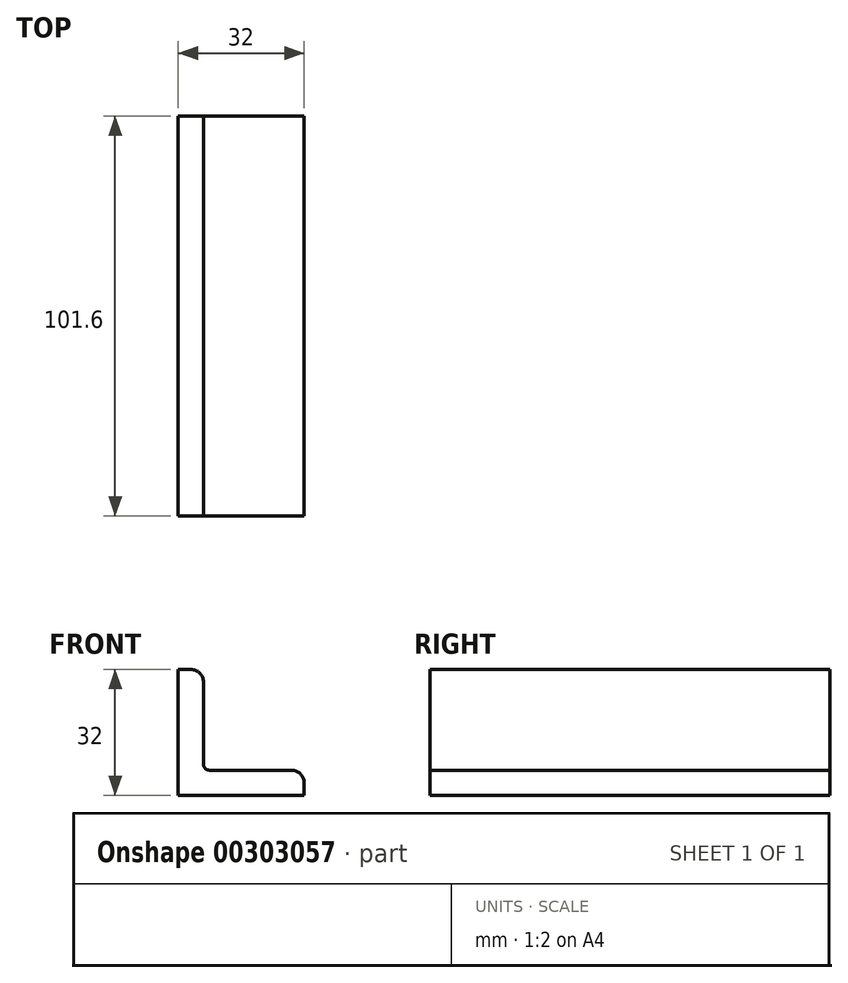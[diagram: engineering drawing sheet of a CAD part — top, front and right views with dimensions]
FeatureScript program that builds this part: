
annotation { "Feature Type Name" : "Feature", "Feature Type Description" : "" }
export const myFeature = defineFeature(function(context is Context, id is Id, definition is map)
    precondition{}
    {
        {
            var Q0;
            Q0=qCreatedBy(makeId("Front.planeOp"),FACE);
            var sketch = newSketch(context, id + "F0", { "sketchPlane" : qUnion([Q0])});
            skLineSegment(sketch, "E0", {"start": v(0, 32) * mm, "end": v(0, 0) * mm});
            skLineSegment(sketch, "E1", {"start": v(0, 0) * mm, "end": v(32, 0) * mm});
            skLineSegment(sketch, "E2", {"start": v(0, 32) * mm, "end": v(3.2, 32) * mm});
            skLineSegment(sketch, "E3", {"start": v(32, 0) * mm, "end": v(32, 3.2) * mm});
            skLineSegment(sketch, "E4", {"start": v(6.4, 28.8) * mm, "end": v(6.4, 8) * mm});
            skLineSegment(sketch, "E5", {"start": v(8, 6.4) * mm, "end": v(28.8, 6.4) * mm});
            skArc(sketch, "E6", {"start": v(6.4, 8) * mm, "mid": v(6.87, 6.87) * mm, "end": v(8, 6.4) * mm});
            skArc(sketch, "E7", {"start": v(28.8, 6.4) * mm, "mid": v(31.06, 5.46) * mm, "end": v(32, 3.2) * mm});
            skArc(sketch, "E8", {"start": v(6.4, 28.8) * mm, "mid": v(5.46, 31.06) * mm, "end": v(3.2, 32) * mm});
            skSolve(sketch);
        }
        {
            var Q0;
            Q0=qSketchRegion(id+"F0",true);
            extrude(context, id + "F1", {"entities" : qUnion([Q0]), "depth" : 101.6 * mm, "symmetric" : true});
        }
    });
